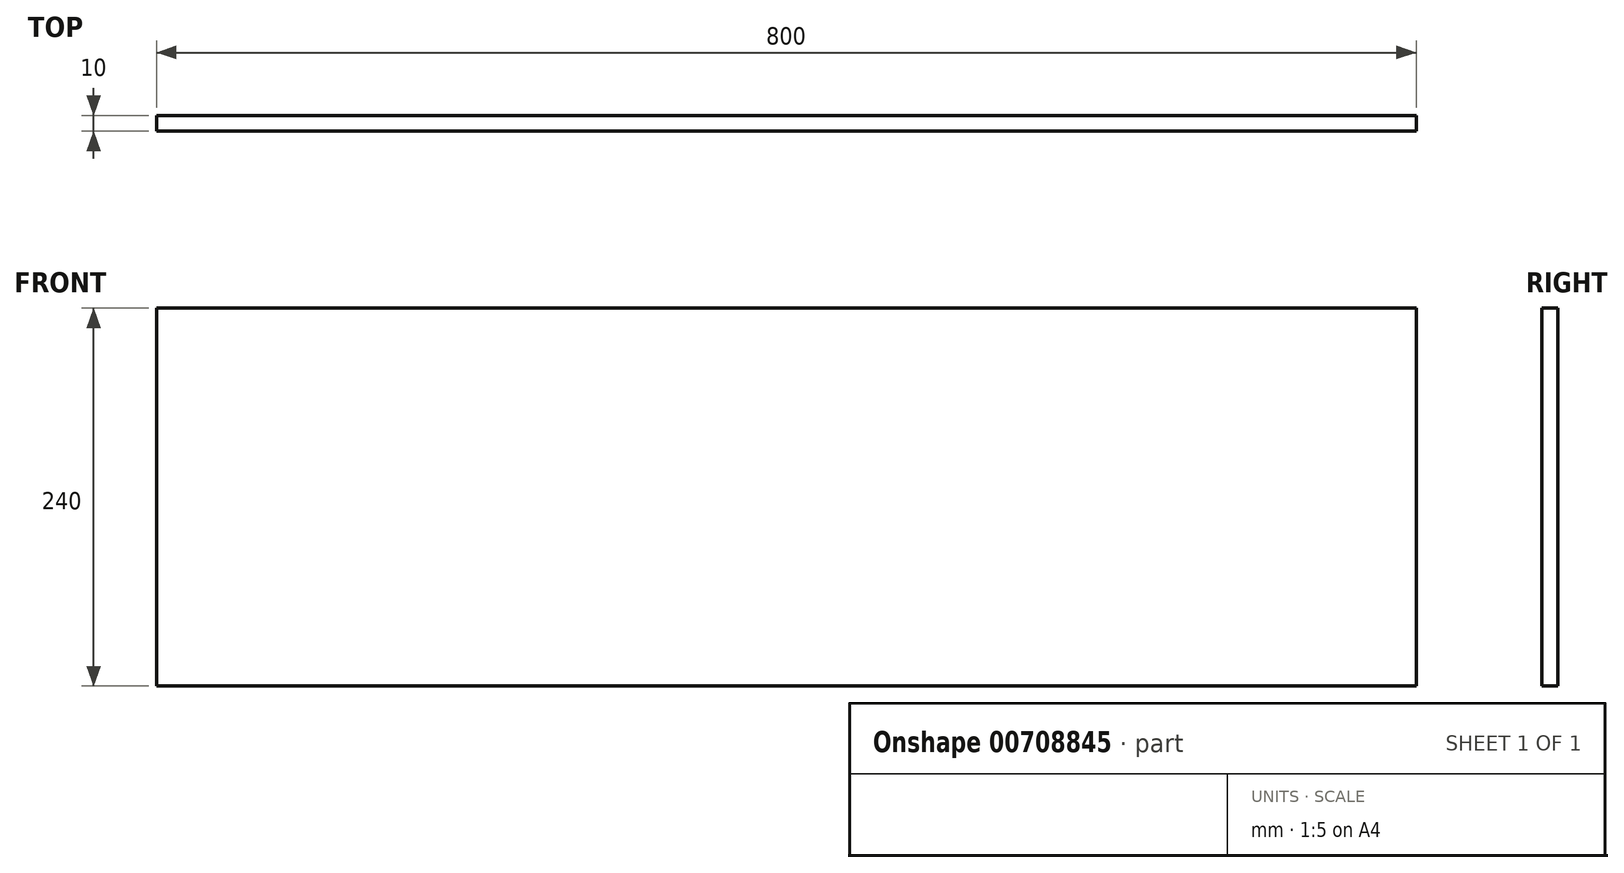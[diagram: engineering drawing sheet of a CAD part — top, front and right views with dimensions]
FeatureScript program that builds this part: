
annotation { "Feature Type Name" : "Feature", "Feature Type Description" : "" }
export const myFeature = defineFeature(function(context is Context, id is Id, definition is map)
    precondition{}
    {
        {
            var Q0;
            Q0=qCreatedBy(makeId("Front.planeOp"),FACE);
            var sketch = newSketch(context, id + "F0", { "sketchPlane" : qUnion([Q0])});
            skLineSegment(sketch, "E0.bottom", {"start": v(400, 120) * mm, "end": v(-400, 120) * mm});
            skLineSegment(sketch, "E0.top", {"start": v(400, -120) * mm, "end": v(-400, -120) * mm});
            skLineSegment(sketch, "E0.left", {"start": v(400, 120) * mm, "end": v(400, -120) * mm});
            skLineSegment(sketch, "E0.right", {"start": v(-400, 120) * mm, "end": v(-400, -120) * mm});
            skPoint(sketch, "E0.middle", {"position": v(0, 0) * mm});
            skSolve(sketch);
        }
        {
            var Q0;
            Q0=makeQuery(id+"F0.imprint","IMPRINT",FACE,{"disambiguationData":[TD([[makeQuery(id+"F0.imprint","IMPRINT",EDGE,{"derivedFrom":sQuery(id+"F0.wireOp",EDGE,"E0.bottom")}),1.0]])]});
            extrude(context, id + "F1", {"entities" : qUnion([Q0]), "depth" : 10 * mm, "offsetDistance" : 25 * mm});
        }
    });
